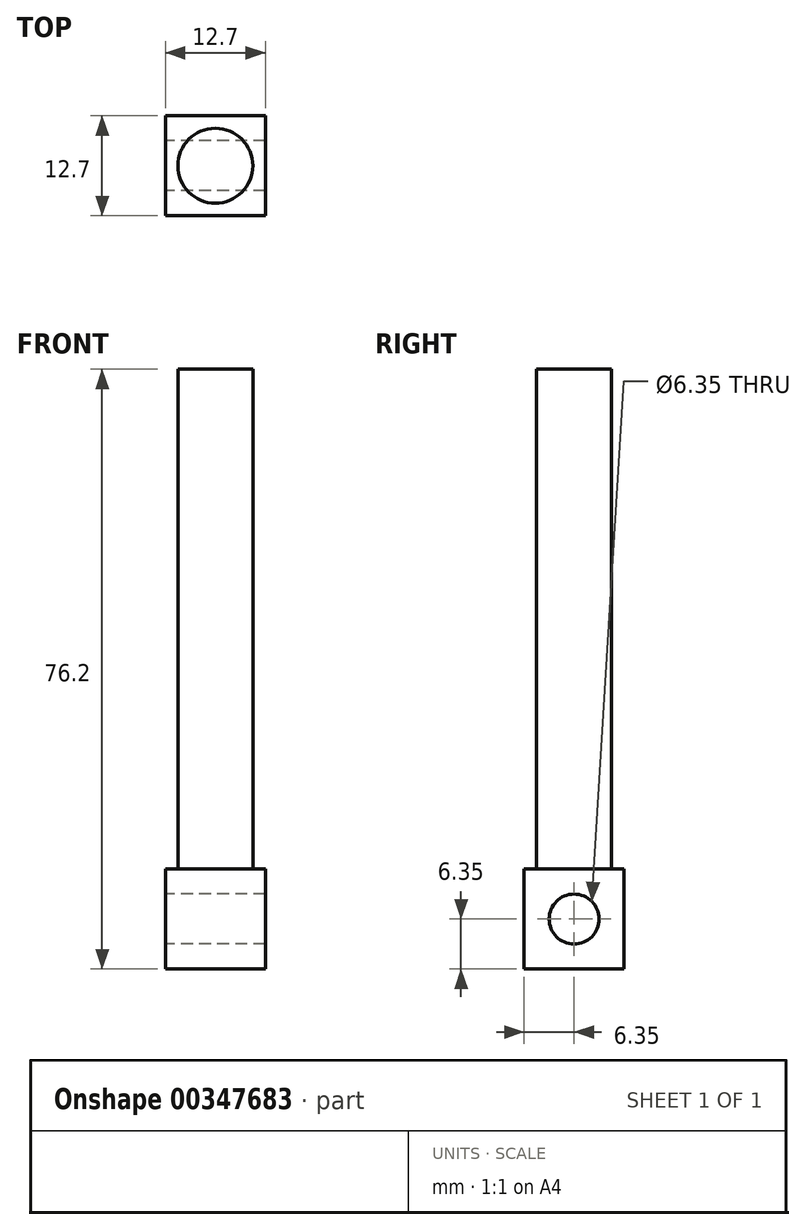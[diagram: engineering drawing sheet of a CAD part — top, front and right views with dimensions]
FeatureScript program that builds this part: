
annotation { "Feature Type Name" : "Feature", "Feature Type Description" : "" }
export const myFeature = defineFeature(function(context is Context, id is Id, definition is map)
    precondition{}
    {
        {
            var Q0;
            Q0=qCreatedBy(makeId("Front.planeOp"),FACE);
            var sketch = newSketch(context, id + "F0", { "sketchPlane" : qUnion([Q0])});
            skLineSegment(sketch, "E0.bottom", {"start": v(6.35, 6.35) * mm, "end": v(-6.35, 6.35) * mm});
            skLineSegment(sketch, "E0.top", {"start": v(6.35, -6.35) * mm, "end": v(-6.35, -6.35) * mm});
            skLineSegment(sketch, "E0.left", {"start": v(6.35, 6.35) * mm, "end": v(6.35, -6.35) * mm});
            skLineSegment(sketch, "E0.right", {"start": v(-6.35, 6.35) * mm, "end": v(-6.35, -6.35) * mm});
            skPoint(sketch, "E0.middle", {"position": v(0, 0) * mm});
            skSolve(sketch);
        }
        {
            var Q0;
            Q0 = qSketchRegion(id + "F0", true);
            extrude(context, id + "F1", {"entities" : qUnion([Q0]), "depth" : 12.7 * mm});
        }
        {
            var Q0;
            Q0=makeQuery(id+"F1.opExtrude","SWEPT_FACE",FACE,{"disambiguationData":[OSD([sQuery(id+"F0.wireOp",EDGE,"E0.bottom")])]});
            var sketch = newSketch(context, id + "F2", { "sketchPlane" : qUnion([Q0])});
            skCircle(sketch, "E1", {"center": v(0, -6.35) * mm, "radius": 4.76 * mm});
            skLineSegment(sketch, "E2", {"start": v(-6.35, -6.35) * mm, "end": v(6.35, -6.35) * mm, "construction": true});
            skSolve(sketch);
        }
        {
            var Q0;
            Q0 = qSketchRegion(id + "F2", true);
            extrude(context, id + "F3", {"entities" : qUnion([Q0]), "operationType" : NewBodyOperationType.ADD, "depth" : 63.5 * mm});
        }
        {
            var Q0;
            Q0=makeQuery(id+"F1.opExtrude","SWEPT_FACE",FACE,{"disambiguationData":[OSD([sQuery(id+"F0.wireOp",EDGE,"E0.right")])]});
            var sketch = newSketch(context, id + "F4", { "sketchPlane" : qUnion([Q0])});
            skLineSegment(sketch, "E3", {"start": v(6.35, -6.35) * mm, "end": v(6.35, 0) * mm, "construction": true});
            skPoint(sketch, "E4", {"position": v(6.35, 6.35) * mm});
            skCircle(sketch, "E5", {"center": v(6.35, 0) * mm, "radius": 3.18 * mm});
            skSolve(sketch);
        }
        {
            var Q0;
            Q0 = qSketchRegion(id + "F4", true);
            extrude(context, id + "F5", {"entities" : qUnion([Q0]), "operationType" : NewBodyOperationType.REMOVE, "endBound" : BoundingType.THROUGH_ALL, "oppositeDirection" : true, "depth" : 25.4 * mm});
        }
    });
